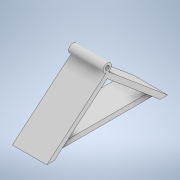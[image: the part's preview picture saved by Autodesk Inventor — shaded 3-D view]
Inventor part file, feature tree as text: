
AUTODESK INVENTOR PART (.ipt)
format: ipt  version: 2021 (Build 250183000, 183)  size: 182,784 bytes
history: native  units: mm
features: extrude x8, sketch x8, projected_geometry x4, plane x1
ambient origin geometry x8: Origin, YZ Plane, XZ Plane, XY Plane, X Axis, Y Axis, Z Axis, Center Point
bodies: Volumenkörper1 (feature_tree)
feature tree (21):
  extrude  "Extrusion1"  Depth=3.5mm
  extrude  "Extrusion2"  Depth=2.0mm
  extrude  "Extrusion3"  Depth=28.5mm TaperAngle=0.0deg
  extrude  "Extrusion4"  Depth=24.0mm TaperAngle=0.0deg
  extrude  "Extrusion5"  TaperAngle=0.0deg  [1 undecoded]
  plane  "Arbeitsebene1"
  extrude  "Extrusion6"  [1 undecoded]
  extrude  "Extrusion7"  Depth=3.5mm TaperAngle=0.0deg
  extrude  "Extrusion8"  TaperAngle=0.0deg  [1 undecoded]
  sketch  "Skizze1"  dims[d0=6.981317mm d1=3.5mm]
  sketch  "Skizze2"  dims[d2=7.0mm d3=2.0mm]
  projected_geometry  "Projizierte Kontur1"
  sketch  "Skizze3"  dims[d4=100.0mm d5=28.5mm d6=0.0mm]
  projected_geometry  "Projizierte Kontur2"
  sketch  "Skizze4"  dims[d7=5.0mm d8=0.0mm d9=24.0mm d10=0.0mm]
  sketch  "Skizze5"  dims[d11=72.5mm d12=0.0mm d13=0.0mm]
  projected_geometry  "Projizierte Kontur3"
  sketch  "Skizze6"  dims[d14=14.5mm d15=0.0mm d16=-2.0mm]
  sketch  "Skizze7"  dims[d17=2.0mm d18=3.5mm d19=0.0mm]
  projected_geometry  "Projizierte Kontur4"
  sketch  "Skizze8"  dims[d20=2.0mm d21=0.0mm d22=0.0mm d23=4.0mm d24=15.0mm d25=0.0mm]
note: 3 required parameter values undecoded (feature->parameter linkage not recoverable at this tier; creation-order binding heuristic only, values carry confidence <= 0.55)
